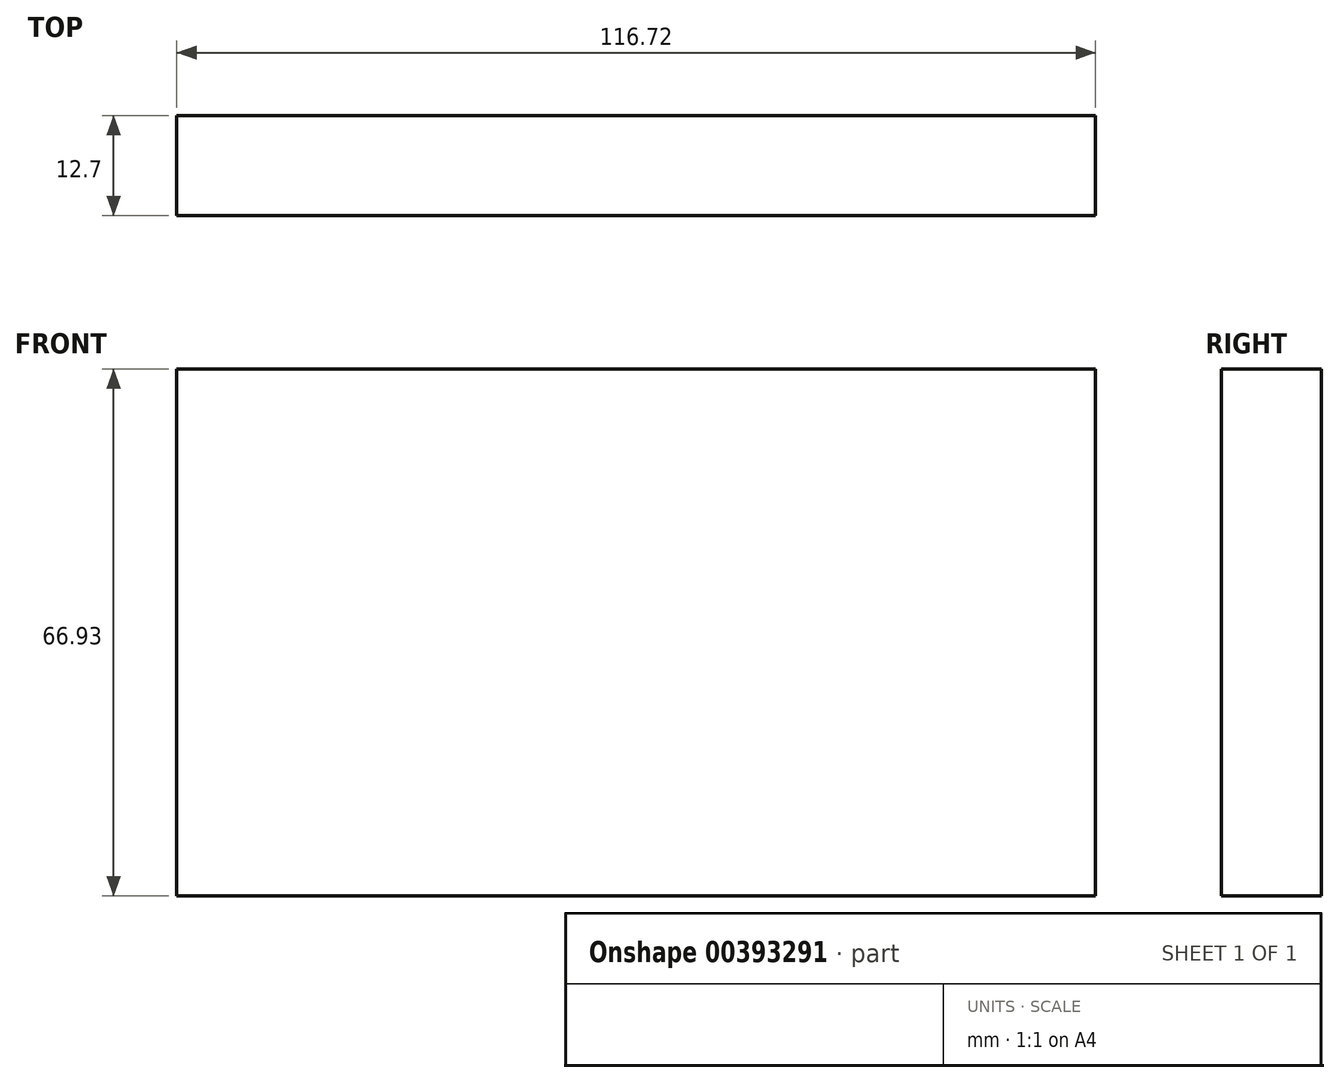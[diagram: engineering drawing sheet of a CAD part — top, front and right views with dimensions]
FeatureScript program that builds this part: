
annotation { "Feature Type Name" : "Feature", "Feature Type Description" : "" }
export const myFeature = defineFeature(function(context is Context, id is Id, definition is map)
    precondition{}
    {
        {
            var Q0;
            Q0=qCreatedBy(makeId("Front.planeOp"),FACE);
            var sketch = newSketch(context, id + "F0", { "sketchPlane" : qUnion([Q0])});
            skLineSegment(sketch, "E0.bottom", {"start": v(-161, -7.13) * mm, "end": v(-44.28, -7.13) * mm});
            skLineSegment(sketch, "E0.top", {"start": v(-161, -74.06) * mm, "end": v(-44.28, -74.06) * mm});
            skLineSegment(sketch, "E0.left", {"start": v(-161, -7.13) * mm, "end": v(-161, -74.06) * mm});
            skLineSegment(sketch, "E0.right", {"start": v(-44.28, -7.13) * mm, "end": v(-44.28, -74.06) * mm});
            skSolve(sketch);
        }
        {
            var Q0;
            Q0=makeQuery(id+"F0.imprint","IMPRINT",FACE,{"disambiguationData":[TD([[makeQuery(id+"F0.imprint","IMPRINT",EDGE,{"derivedFrom":sQuery(id+"F0.wireOp",EDGE,"E0.bottom")}),-1.0]])]});
            extrude(context, id + "F1", {"entities" : qUnion([Q0]), "depth" : 12.7 * mm});
        }
    });
